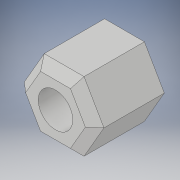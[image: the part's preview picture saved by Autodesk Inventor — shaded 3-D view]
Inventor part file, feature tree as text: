
AUTODESK INVENTOR PART (.ipt)
format: ipt  version: 2018 (Build 220112000, 112)  size: 108,032 bytes
history: native  units: in
note: dims shown in document units (in); Inventor stores cm internally (conversion verified against a paired STEP export)
features: extrude x2, sketch x2, chamfer x1
ambient origin geometry x8: Origin, YZ Plane, XZ Plane, XY Plane, X Axis, Y Axis, Z Axis, Center Point
bodies: Solid1 (feature_tree)
feature tree (5):
  extrude  "Extrusion1"  Depth=0.5in TaperAngle=0.0deg
  extrude  "Extrusion2"  Depth=0.5in TaperAngle=0.0deg
  chamfer  "Chamfer1"  Distance=0.125in Angle=45.0deg
  sketch  "Sketch1"  dims[d0=0.5in d1=0.5in d2=0.0in]
  sketch  "Sketch2"  dims[d3=0.25in d4=0.5in d5=0.0in d6=0.0625in d7=0.125in d8=45.0deg]
